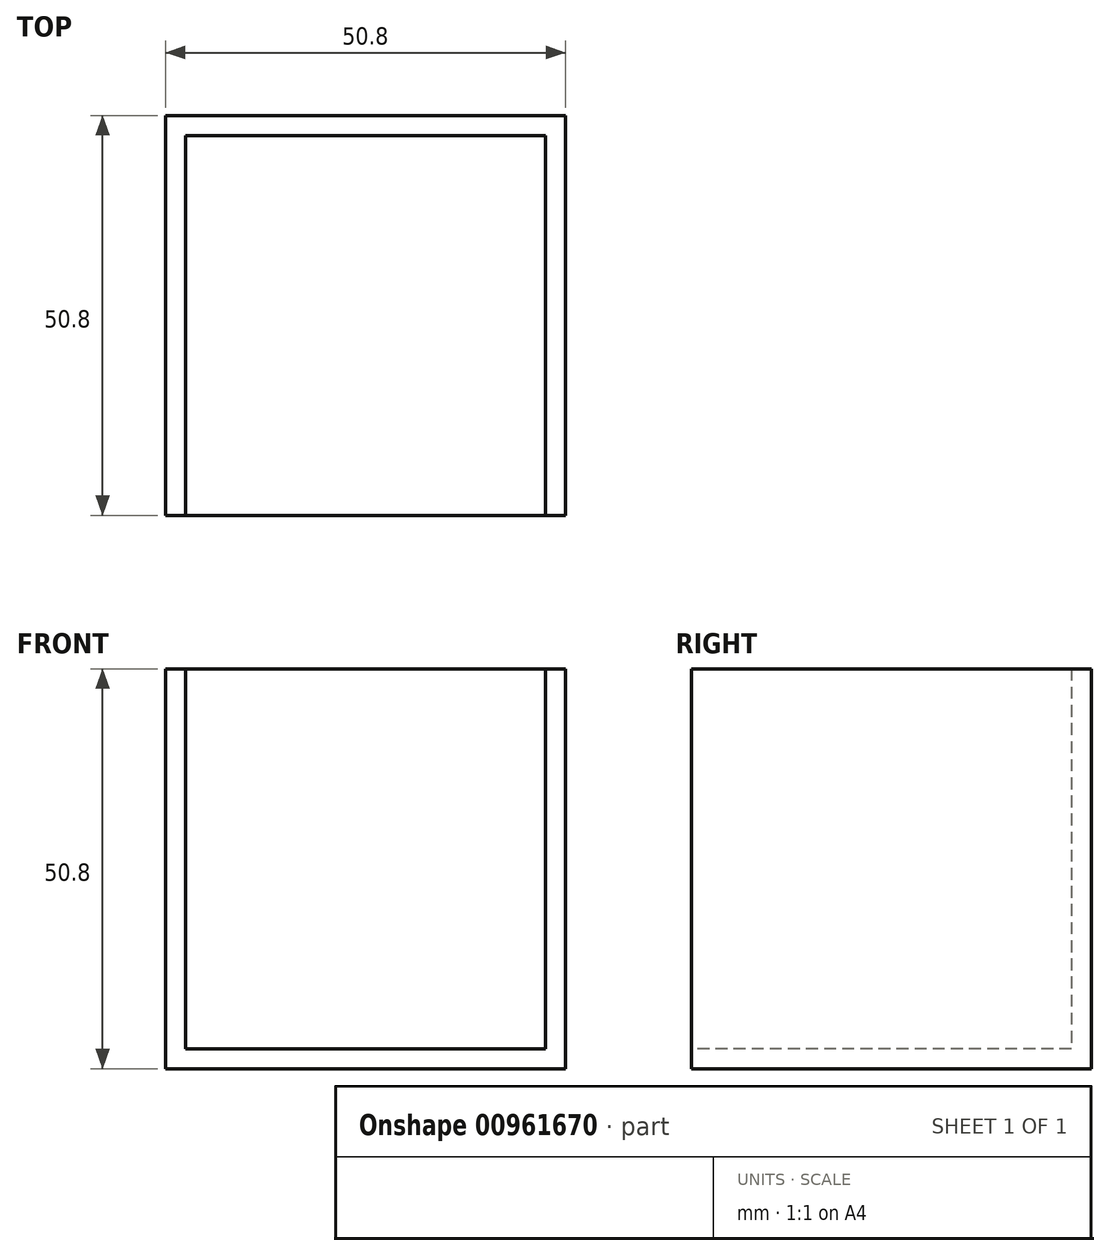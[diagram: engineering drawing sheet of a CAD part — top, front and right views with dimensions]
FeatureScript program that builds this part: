
annotation { "Feature Type Name" : "Feature", "Feature Type Description" : "" }
export const myFeature = defineFeature(function(context is Context, id is Id, definition is map)
    precondition{}
    {
        {
            var Q0;
            Q0=qCreatedBy(makeId("Top.planeOp"),FACE);
            var sketch = newSketch(context, id + "F0", { "sketchPlane" : qUnion([Q0])});
            skLineSegment(sketch, "E0.bottom", {"start": v(0, 0) * mm, "end": v(50.8, 0) * mm});
            skLineSegment(sketch, "E0.top", {"start": v(0, -50.8) * mm, "end": v(50.8, -50.8) * mm});
            skLineSegment(sketch, "E0.left", {"start": v(0, 0) * mm, "end": v(0, -50.8) * mm});
            skLineSegment(sketch, "E0.right", {"start": v(50.8, 0) * mm, "end": v(50.8, -50.8) * mm});
            skSolve(sketch);
        }
        {
            var Q0;
            Q0=makeQuery(id+"F0.imprint","IMPRINT",FACE,{"disambiguationData":[TD([[makeQuery(id+"F0.imprint","IMPRINT",EDGE,{"derivedFrom":sQuery(id+"F0.wireOp",EDGE,"E0.bottom")}),-1.0]])]});
            extrude(context, id + "F1", {"entities" : qUnion([Q0]), "depth" : 50.8 * mm, "offsetDistance" : 25.4 * mm});
        }
        {
            var Q0;
            Q0=makeQuery(id+"F1.opExtrude","SWEPT_FACE",FACE,{"disambiguationData":[OSD([sQuery(id+"F0.wireOp",EDGE,"E0.top")])]});
            var Q1;
            Q1=makeQuery(id+"F1.opExtrude","CAP_FACE",FACE,{"disambiguationData":[OSD([sQuery(id+"F0.wireOp",EDGE,"E0.bottom"),sQuery(id+"F0.wireOp",EDGE,"E0.top"),sQuery(id+"F0.wireOp",EDGE,"E0.left"),sQuery(id+"F0.wireOp",EDGE,"E0.right")])],"isStart":false});
            shell(context, id + "F2", {"entities" : qUnion([Q0, Q1]), "thickness" : 2.54 * mm});
        }
    });
